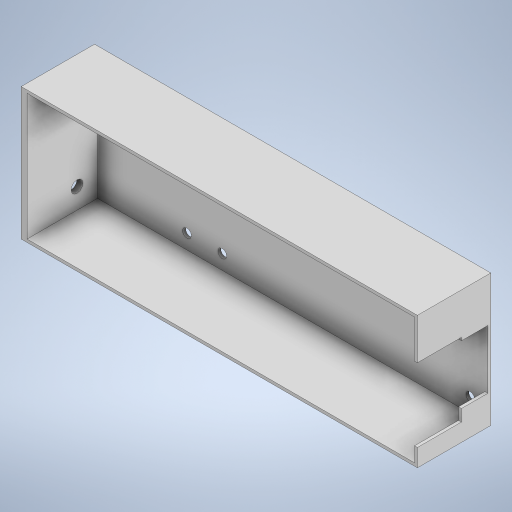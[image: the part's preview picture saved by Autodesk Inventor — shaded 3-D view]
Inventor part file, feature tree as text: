
AUTODESK INVENTOR PART (.ipt)
format: ipt  version: 2023 (Build 270158000, 158)  size: 310,272 bytes
history: native  units: mm
features: extrude x5, sketch x5
ambient origin geometry x8: Origin, YZ Plane, XZ Plane, XY Plane, X Axis, Y Axis, Z Axis, Center Point
bodies: Solid1 (feature_tree)
feature tree (10):
  extrude  "Extrusion1"  Depth=1.0mm
  extrude  "Extrusion2"  Depth=1.0mm
  extrude  "Extrusion3"  Depth=6.0mm
  sketch  "Sketch4"  dims[d10=3.0mm d11=3.0mm]
  extrude  "Extrusion4"  Depth=3.0mm
  extrude  "Extrusion5"  Depth=6.0mm
  sketch  "Sketch1"  dims[d0=135.0mm d2=1.0mm]
  sketch  "Sketch2"  dims[d3=1.0mm d7=3.0mm]
  sketch  "Sketch3"  dims[d8=6.0mm d9=6.0mm]
  sketch  "Sketch5"  dims[d14=3.0mm d15=6.0mm d16=6.0mm d17=6.0mm d18=6.0mm d19=12.0mm d20=32.5mm d21=3.0mm d22=3.0mm d23=6.0mm d24=6.0mm d25=32.5mm d26=12.0mm d27=1.0mm d28=0.0mm d29=25.0mm d30=10.0mm d31=10.0mm d32=20.0mm d33=6.0mm d34=25.0mm d35=1.0mm d36=0.0mm d37=1.0mm d38=0.0mm d39=25.0mm d40=12.0mm d42=8.0mm d43=2.0mm d44=0.0mm d45=1.0mm d46=0.0mm d47=4.0mm d48=4.0mm d49=8.0mm]
